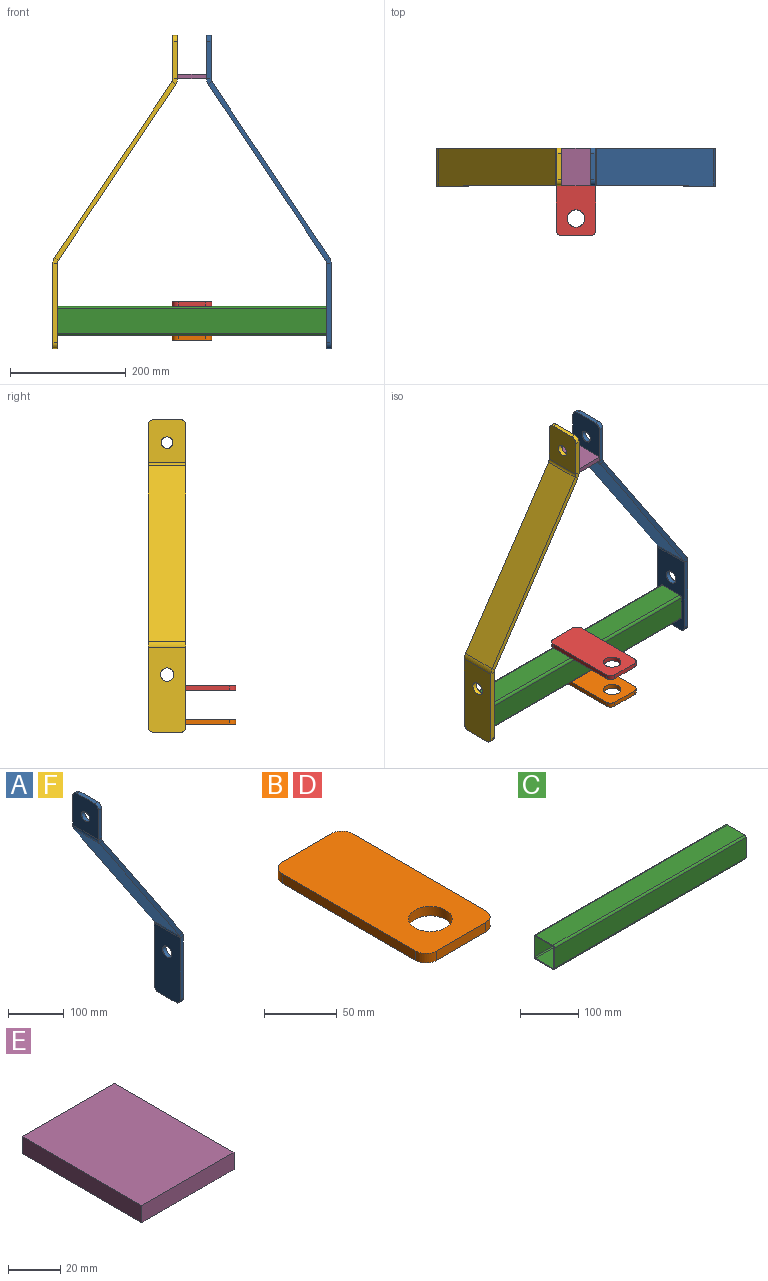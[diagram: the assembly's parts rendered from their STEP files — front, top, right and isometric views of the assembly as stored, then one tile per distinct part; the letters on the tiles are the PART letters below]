
ASSEMBLY  parts=6 mates=5
PART A: 28 faces, bbox 215x65x540 mm
  f0: plane 136.97x8mm, normal (0,1,0), area 1095.7mm2, adj f4,f5,f6,f25
  f1: plane 136.97x8mm, normal (0,-1,0), area 1095.7mm2, adj f4,f5,f7,f24
  f2: cylinder r=11.5mm len=23mm, axis (1,0,0), area 578.1mm2, adj f4,f5
  f3: plane 45x8mm, normal (0,0,-1), area 360mm2, adj f4,f5,f6,f7
  f4: plane 146.97x65mm, normal (1,0,0), area 9094.5mm2, adj f0,f1,f2,f3,f6,f7,f26
  f5: plane 146.97x65mm, normal (-1,0,0), area 9094.5mm2, adj f0,f1,f2,f3,f6,f7,f27
  f6: cylinder r=10mm len=10mm, axis (-1,0,0), area 125.7mm2, adj f0,f3,f4,f5
  f7: cylinder r=10mm len=10mm, axis (1,0,0), area 125.7mm2, adj f1,f3,f4,f5
  f8: plane 307.38x208.94mm, normal (0,1,0), area 2914.2mm2, adj f10,f11,f21,f25
  f9: plane 307.38x208.94mm, normal (0,-1,0), area 2914.2mm2, adj f10,f11,f20,f24
  f10: plane 302.94x202.29mm, normal (0.83,0,0.56), area 23677.5mm2, adj f8,f9,f23,f26
  f11: plane 302.94x202.29mm, normal (-0.83,0,-0.56), area 23677.5mm2, adj f8,f9,f22,f27
  f12: plane 64.54x8mm, normal (0,1,0), area 516.3mm2, adj f16,f17,f18,f21
  f13: plane 45x8mm, normal (0,0,1), area 360mm2, adj f16,f17,f18,f19
  f14: plane 64.54x8mm, normal (0,-1,0), area 516.3mm2, adj f16,f17,f19,f20
  f15: cylinder r=10mm len=20mm, axis (1,0,0), area 502.7mm2, adj f16,f17
  f16: plane 74.54x65mm, normal (1,0,0), area 4488.2mm2, adj f12,f13,f14,f15,f18,f19,f23
  f17: plane 74.54x65mm, normal (-1,0,0), area 4488.2mm2, adj f12,f13,f14,f15,f18,f19,f22
  f18: cylinder r=10mm len=10mm, axis (1,0,0), area 125.7mm2, adj f12,f13,f16,f17
  f19: cylinder r=10mm len=10mm, axis (-1,0,0), area 125.7mm2, adj f13,f14,f16,f17
  f20: plane 10x9.68mm, normal (0,-1,0), area 65.9mm2, adj f9,f14,f22,f23
  f21: plane 10x9.68mm, normal (0,1,0), area 65.9mm2, adj f8,f12,f22,f23
  f22: cylinder r=18mm len=65mm, axis (0,-1,0), area 688.8mm2, adj f11,f17,f20,f21
  f23: cylinder r=10mm len=65mm, axis (0,-1,0), area 382.7mm2, adj f10,f16,f20,f21
  f24: plane 10x9.68mm, normal (0,-1,0), area 65.9mm2, adj f1,f9,f26,f27
  f25: plane 10x9.68mm, normal (0,1,0), area 65.9mm2, adj f0,f8,f26,f27
  f26: cylinder r=18mm len=65mm, axis (0,-1,0), area 688.8mm2, adj f4,f10,f24,f25
  f27: cylinder r=10mm len=65mm, axis (0,-1,0), area 382.7mm2, adj f5,f11,f24,f25
PART B: 11 faces, bbox 68x150x8 mm
  f0: plane 130x8mm, normal (-1,0,0), area 1040mm2, adj f5,f6,f8,f9
  f1: plane 48x8mm, normal (0,-1,0), area 384mm2, adj f5,f6,f7,f9
  f2: plane 130x8mm, normal (1,0,0), area 1040mm2, adj f5,f6,f7,f10
  f3: cylinder r=15mm len=30mm, axis (0,0,1), area 754mm2, adj f5,f6
  f4: plane 48x8mm, normal (0,1,0), area 384mm2, adj f5,f6,f8,f10
  f5: plane 150x68mm, normal (0,0,1), area 9407.3mm2, adj f0,f1,f2,f3,f4,f7,f8,f9
  f6: plane 150x68mm, normal (0,0,-1), area 9407.3mm2, adj f0,f1,f2,f3,f4,f7,f8,f9
  f7: cylinder r=10mm len=10mm, axis (0,0,-1), area 125.7mm2, adj f1,f2,f5,f6
  f8: cylinder r=10mm len=10mm, axis (0,0,-1), area 125.7mm2, adj f0,f4,f5,f6
  f9: cylinder r=10mm len=10mm, axis (0,0,1), area 125.7mm2, adj f0,f1,f5,f6
  f10: cylinder r=10mm len=10mm, axis (0,0,1), area 125.7mm2, adj f2,f4,f5,f6
PART C: 18 faces, bbox 464x50x50 mm
  f0: plane 464x42mm, normal (0,1,0), area 19488mm2, adj f1,f7,f8,f9
  f1: cylinder r=2.02mm len=464mm, axis (1,0,0), area 1453.8mm2, adj f0,f2,f8,f9
  f2: plane 464x42mm, normal (0,0,-1), area 19488mm2, adj f1,f3,f8,f9
  f3: cylinder r=2.02mm len=464mm, axis (1,0,0), area 1453.8mm2, adj f2,f4,f8,f9
  f4: plane 464x42mm, normal (0,-1,0), area 19488mm2, adj f3,f5,f8,f9
  f5: cylinder r=2.02mm len=464mm, axis (1,0,0), area 1453.8mm2, adj f4,f6,f8,f9
  f6: plane 464x42mm, normal (0,0,1), area 19488mm2, adj f5,f7,f8,f9
  f7: cylinder r=2.02mm len=464mm, axis (1,0,0), area 1453.8mm2, adj f0,f6,f8,f9
  f8: plane 50x50mm, normal (-1,0,0), area 373.8mm2, adj f0,f1,f2,f3,f4,f5,f6,f7
  f9: plane 50x50mm, normal (1,0,0), area 373.8mm2, adj f0,f1,f2,f3,f4,f5,f6,f7
  f10: plane 464x42mm, normal (0,1,0), area 19488mm2, adj f8,f9,f11,f17
  f11: cylinder r=4mm len=464mm, axis (1,0,0), area 2915.4mm2, adj f8,f9,f10,f12
  f12: plane 464x42mm, normal (0,0,1), area 19488mm2, adj f8,f9,f11,f13
  f13: cylinder r=4mm len=464mm, axis (1,0,0), area 2915.4mm2, adj f8,f9,f12,f14
  f14: plane 464x42mm, normal (0,-1,0), area 19488mm2, adj f8,f9,f13,f15
  f15: cylinder r=4mm len=464mm, axis (1,0,0), area 2915.4mm2, adj f8,f9,f14,f16
  f16: plane 464x42mm, normal (0,0,-1), area 19488mm2, adj f8,f9,f15,f17
  f17: cylinder r=4mm len=464mm, axis (1,0,0), area 2915.4mm2, adj f8,f9,f10,f16
PART D: same geometry as B
PART E: 6 faces, bbox 50x65x8 mm
  f0: plane 50x8mm, normal (0,1,0), area 400mm2, adj f1,f3,f4,f5
  f1: plane 65x8mm, normal (-1,0,0), area 520mm2, adj f0,f2,f4,f5
  f2: plane 50x8mm, normal (0,-1,0), area 400mm2, adj f1,f3,f4,f5
  f3: plane 65x8mm, normal (1,0,0), area 520mm2, adj f0,f2,f4,f5
  f4: plane 65x50mm, normal (0,0,1), area 3250mm2, adj f0,f1,f2,f3
  f5: plane 65x50mm, normal (0,0,-1), area 3250mm2, adj f0,f1,f2,f3
PART F: same geometry as A
PLACE A t=(0,25,9.85)mm
PLACE B t=(0,26.62,-58)mm
PLACE C t=(0,25,0)mm
PLACE D t=(0,26.62,0)mm
PLACE E t=(0,25,15.3)mm
PLACE F rot(axis=(0,0,1),180deg) t=(0,25,9.85)mm
MATE fastened D.f3 <-> B.f3  axis (0,0,-1) through (0,-63.38,25)mm
MATE fastened C.f12 <-> D.f6  axis (0,0,1) through (0,25,25)mm
MATE fastened A.f17 <-> E.f3  axis (-1,0,0) through (25,25,417.85)mm
MATE fastened C.f9 <-> A.f5  axis (1,0,0) through (232,25,0)mm
MATE fastened F.f15 <-> A.f15  axis (1,0,0) through (-25,25,452.39)mm
